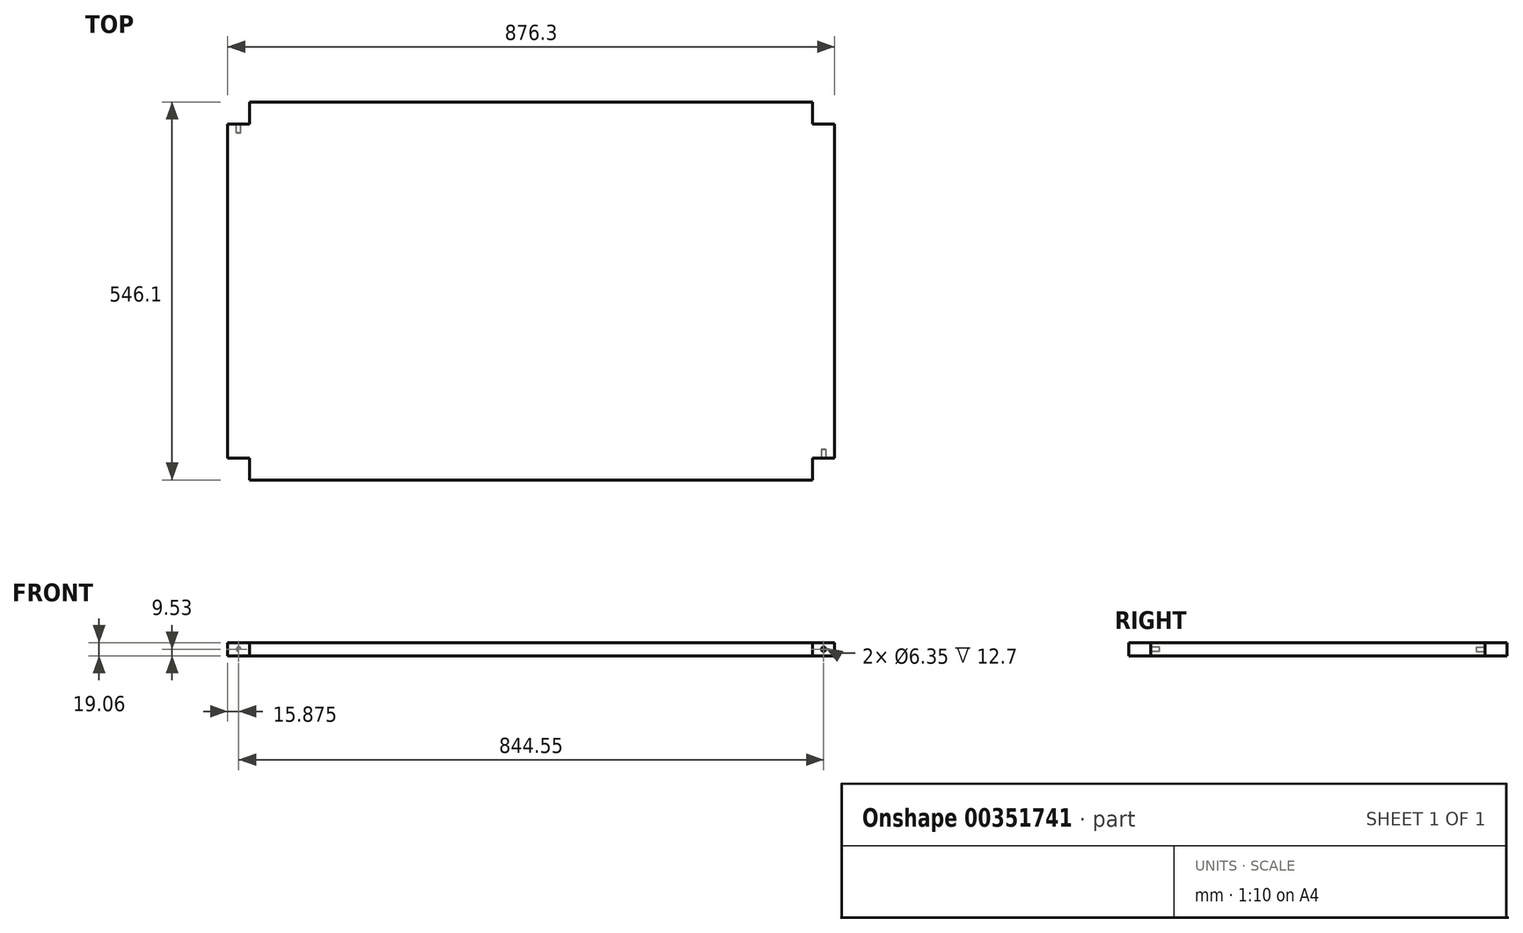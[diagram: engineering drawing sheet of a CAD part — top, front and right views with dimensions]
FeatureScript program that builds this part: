
annotation { "Feature Type Name" : "Feature", "Feature Type Description" : "" }
export const myFeature = defineFeature(function(context is Context, id is Id, definition is map)
    precondition{}
    {
        {
            var Q0;
            Q0=qCreatedBy(makeId("Top.planeOp"),FACE);
            var sketch = newSketch(context, id + "F0", { "sketchPlane" : qUnion([Q0])});
            skLineSegment(sketch, "E0.bottom", {"start": v(-406.4, 273.05) * mm, "end": v(406.4, 273.05) * mm});
            skLineSegment(sketch, "E0.top", {"start": v(-406.4, -273.05) * mm, "end": v(406.4, -273.05) * mm});
            skLineSegment(sketch, "E0.left", {"start": v(-438.15, 241.3) * mm, "end": v(-438.15, -241.3) * mm});
            skLineSegment(sketch, "E0.right", {"start": v(438.15, 241.3) * mm, "end": v(438.15, -241.3) * mm});
            skPoint(sketch, "E0.middle", {"position": v(0, 0) * mm});
            skLineSegment(sketch, "E1", {"start": v(-438.15, 241.3) * mm, "end": v(-406.4, 241.3) * mm});
            skLineSegment(sketch, "E2.left", {"start": v(-406.4, 241.3) * mm, "end": v(-406.4, 273.05) * mm});
            skLineSegment(sketch, "E3.top", {"start": v(438.15, 241.3) * mm, "end": v(406.4, 241.3) * mm});
            skLineSegment(sketch, "E3.right", {"start": v(406.4, 273.05) * mm, "end": v(406.4, 241.3) * mm});
            skPoint(sketch, "E4.orphan", {"position": v(438.15, 273.05) * mm});
            skPoint(sketch, "E5.orphan", {"position": v(-438.15, 273.05) * mm});
            skLineSegment(sketch, "E6.top", {"start": v(-438.15, -241.3) * mm, "end": v(-406.4, -241.3) * mm});
            skLineSegment(sketch, "E6.right", {"start": v(-406.4, -273.05) * mm, "end": v(-406.4, -241.3) * mm});
            skPoint(sketch, "E7.orphan", {"position": v(-438.15, -273.05) * mm});
            skLineSegment(sketch, "E8.top", {"start": v(438.15, -241.3) * mm, "end": v(406.4, -241.3) * mm});
            skLineSegment(sketch, "E8.right", {"start": v(406.4, -273.05) * mm, "end": v(406.4, -241.3) * mm});
            skPoint(sketch, "E9.orphan", {"position": v(438.15, -273.05) * mm});
            skSolve(sketch);
        }
        {
            var Q0;
            Q0=makeQuery(id+"F0.imprint","IMPRINT",FACE,{"disambiguationData":[TD([[makeQuery(id+"F0.imprint","IMPRINT",EDGE,{"derivedFrom":sQuery(id+"F0.wireOp",EDGE,"E0.bottom")}),-1.0]])]});
            extrude(context, id + "F1", {"entities" : qUnion([Q0]), "endBound" : BoundingType.SYMMETRIC, "depth" : 19.05 * mm});
        }
        {
            var Q0;
            Q0=makeQuery(id+"F1.opExtrude","SWEPT_FACE",FACE,{"disambiguationData":[OSD([sQuery(id+"F0.wireOp",EDGE,"E1")])]});
            var sketch = newSketch(context, id + "F2", { "sketchPlane" : qUnion([Q0])});
            skCircle(sketch, "E10", {"center": v(422.27, 0) * mm, "radius": 3.18 * mm});
            skSolve(sketch);
        }
        {
            var Q0;
            Q0 = qSketchRegion(id + "F2", true);
            extrude(context, id + "F3", {"entities" : qUnion([Q0]), "operationType" : NewBodyOperationType.REMOVE, "oppositeDirection" : true, "depth" : 12.7 * mm, "offsetDistance" : 25.4 * mm});
        }
        {
            var Q0;
            Q0=makeQuery(id+"F1.opExtrude","SWEPT_FACE",FACE,{"disambiguationData":[OSD([sQuery(id+"F0.wireOp",EDGE,"E8.top")])]});
            var sketch = newSketch(context, id + "F4", { "sketchPlane" : qUnion([Q0])});
            skCircle(sketch, "E11", {"center": v(422.27, 0) * mm, "radius": 3.18 * mm});
            skSolve(sketch);
        }
        {
            var Q0;
            Q0 = qSketchRegion(id + "F4", true);
            extrude(context, id + "F5", {"entities" : qUnion([Q0]), "operationType" : NewBodyOperationType.REMOVE, "oppositeDirection" : true, "depth" : 12.7 * mm, "offsetDistance" : 25.4 * mm});
        }
    });
